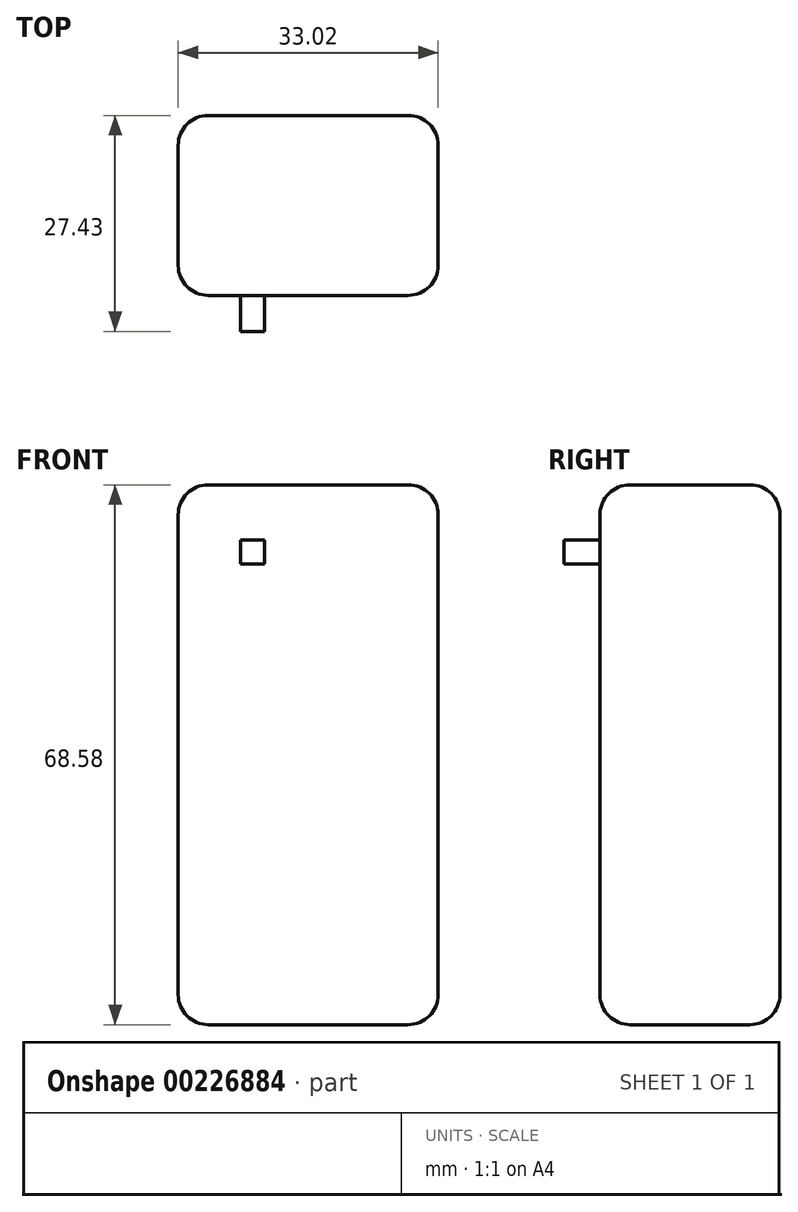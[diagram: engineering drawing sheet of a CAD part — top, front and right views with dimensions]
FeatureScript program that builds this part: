
annotation { "Feature Type Name" : "Feature", "Feature Type Description" : "" }
export const myFeature = defineFeature(function(context is Context, id is Id, definition is map)
    precondition{}
    {
        {
            var Q0;
            Q0=qCreatedBy(makeId("Front.planeOp"),FACE);
            var sketch = newSketch(context, id + "F0", { "sketchPlane" : qUnion([Q0])});
            skLineSegment(sketch, "E0.bottom", {"start": v(0, 0) * mm, "end": v(33.02, 0) * mm});
            skLineSegment(sketch, "E0.top", {"start": v(0, 68.58) * mm, "end": v(33.02, 68.58) * mm});
            skLineSegment(sketch, "E0.left", {"start": v(0, 0) * mm, "end": v(0, 68.58) * mm});
            skLineSegment(sketch, "E0.right", {"start": v(33.02, 0) * mm, "end": v(33.02, 68.58) * mm});
            skSolve(sketch);
        }
        {
            var Q0;
            Q0=qSketchRegion(id+"F0",true);
            extrude(context, id + "F1", {"entities" : qUnion([Q0]), "depth" : 22.86 * mm});
        }
        {
            var Q0;
            Q0=makeQuery(id+"F1.opExtrude","CAP_EDGE",EDGE,{"disambiguationData":[OSD([sQuery(id+"F0.wireOp",EDGE,"E0.right")])],"isStart":false});
            var Q1;
            Q1=makeQuery(id+"F1.opExtrude","SWEPT_EDGE",EDGE,{"disambiguationData":[OSD([sQuery(id+"F0.wireOp",EDGE,"E0.top"),sQuery(id+"F0.wireOp",EDGE,"E0.right")])]});
            var Q2;
            Q2=makeQuery(id+"F1.opExtrude","CAP_EDGE",EDGE,{"disambiguationData":[OSD([sQuery(id+"F0.wireOp",EDGE,"E0.top")])],"isStart":false});
            var Q3;
            Q3=makeQuery(id+"F1.opExtrude","CAP_EDGE",EDGE,{"disambiguationData":[OSD([sQuery(id+"F0.wireOp",EDGE,"E0.left")])],"isStart":false});
            var Q4;
            Q4=makeQuery(id+"F1.opExtrude","CAP_EDGE",EDGE,{"disambiguationData":[OSD([sQuery(id+"F0.wireOp",EDGE,"E0.bottom")])],"isStart":false});
            var Q5;
            Q5=makeQuery(id+"F1.opExtrude","SWEPT_EDGE",EDGE,{"disambiguationData":[OSD([sQuery(id+"F0.wireOp",EDGE,"E0.bottom"),sQuery(id+"F0.wireOp",EDGE,"E0.right")])]});
            var Q6;
            Q6=makeQuery(id+"F1.opExtrude","CAP_EDGE",EDGE,{"disambiguationData":[OSD([sQuery(id+"F0.wireOp",EDGE,"E0.right")])],"isStart":true});
            var Q7;
            Q7=makeQuery(id+"F1.opExtrude","CAP_EDGE",EDGE,{"disambiguationData":[OSD([sQuery(id+"F0.wireOp",EDGE,"E0.bottom")])],"isStart":true});
            var Q8;
            Q8=makeQuery(id+"F1.opExtrude","CAP_EDGE",EDGE,{"disambiguationData":[OSD([sQuery(id+"F0.wireOp",EDGE,"E0.left")])],"isStart":true});
            var Q9;
            Q9=makeQuery(id+"F1.opExtrude","SWEPT_FACE",FACE,{"disambiguationData":[OSD([sQuery(id+"F0.wireOp",EDGE,"E0.left")])]});
            var Q10;
            Q10=makeQuery(id+"F1.opExtrude","SWEPT_FACE",FACE,{"disambiguationData":[OSD([sQuery(id+"F0.wireOp",EDGE,"E0.top")])]});
            fillet(context, id + "F2", {"entities" : qUnion([Q0, Q1, Q2, Q3, Q4, Q5, Q6, Q7, Q8, Q9, Q10]), "radius" : 3.8 * mm, "tangentPropagation" : true, "allowEdgeOverflow" : false});
        }
        {
            var Q0;
            Q0=makeQuery(id+"F1.opExtrude","CAP_FACE",FACE,{"disambiguationData":[OSD([sQuery(id+"F0.wireOp",EDGE,"E0.bottom"),sQuery(id+"F0.wireOp",EDGE,"E0.top"),sQuery(id+"F0.wireOp",EDGE,"E0.left"),sQuery(id+"F0.wireOp",EDGE,"E0.right")])],"isStart":false});
            var sketch = newSketch(context, id + "F3", { "sketchPlane" : qUnion([Q0])});
            skLineSegment(sketch, "E1.bottom", {"start": v(7.9, 61.57) * mm, "end": v(10.98, 61.57) * mm});
            skLineSegment(sketch, "E1.top", {"start": v(7.9, 58.5) * mm, "end": v(10.98, 58.5) * mm});
            skLineSegment(sketch, "E1.left", {"start": v(7.9, 61.57) * mm, "end": v(7.9, 58.5) * mm});
            skLineSegment(sketch, "E1.right", {"start": v(10.98, 61.57) * mm, "end": v(10.98, 58.5) * mm});
            skSolve(sketch);
        }
        {
            var Q0;
            Q0=qSketchRegion(id+"F3",true);
            extrude(context, id + "F4", {"entities" : qUnion([Q0]), "operationType" : NewBodyOperationType.ADD, "depth" : 4.57 * mm});
        }
    });
